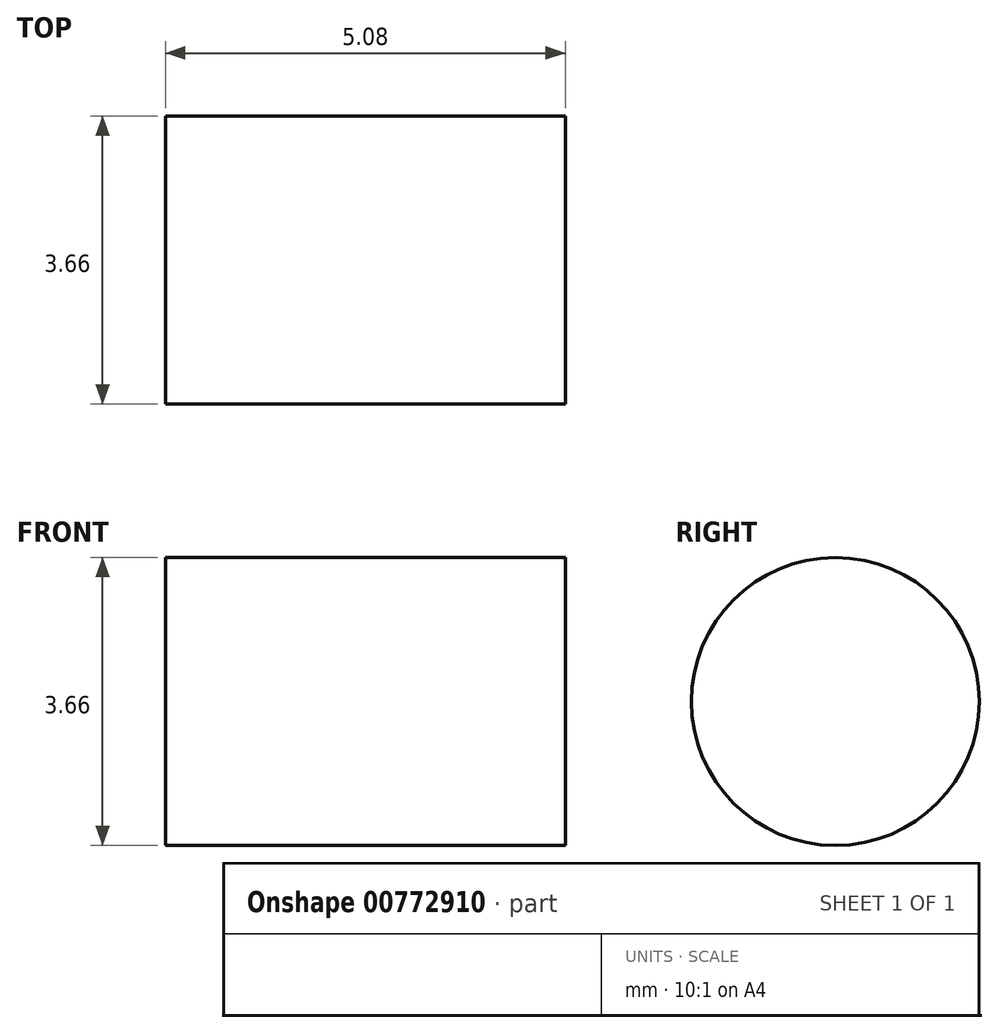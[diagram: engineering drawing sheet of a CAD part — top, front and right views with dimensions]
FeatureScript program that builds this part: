
annotation { "Feature Type Name" : "Feature", "Feature Type Description" : "" }
export const myFeature = defineFeature(function(context is Context, id is Id, definition is map)
    precondition{}
    {
        {
            var Q0;
            Q0=qCreatedBy(makeId("Right.planeOp"),FACE);
            var sketch = newSketch(context, id + "F0", { "sketchPlane" : qUnion([Q0])});
            skCircle(sketch, "E0", {"center": v(51.36, 22.25) * mm, "radius": 1.83 * mm});
            skSolve(sketch);
        }
        {
            var Q0;
            Q0 = qSketchRegion(id + "F0", true);
            extrude(context, id + "F1", {"entities" : qUnion([Q0]), "depth" : 5.08 * mm, "offsetDistance" : 25.4 * mm});
        }
    });
